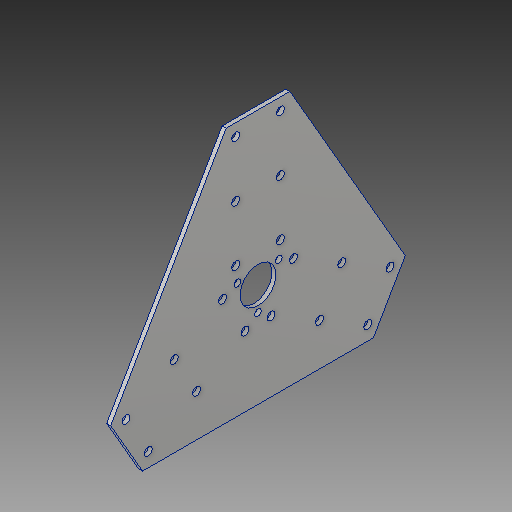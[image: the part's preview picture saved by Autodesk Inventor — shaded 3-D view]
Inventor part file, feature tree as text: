
AUTODESK INVENTOR PART (.ipt)
format: ipt  version: 2019 (Build 230136000, 136)  size: 217,600 bytes
history: native  units: in
note: dims shown in document units (in); Inventor stores cm internally (conversion verified against a paired STEP export)
features: extrude x3, sketch x3, chamfer x1, fillet x1, pattern_circular x1
ambient origin geometry x8: Origin, YZ Plane, XZ Plane, XY Plane, X Axis, Y Axis, Z Axis, Center Point
bodies: Body1 (feature_tree)
feature tree (9):
  extrude  "Extrusion2"  Depth=8.0in
  extrude  "Extrusion3"  Depth=0.125in
  extrude  "Extrusion4"  Depth=0.125in TaperAngle=360.0deg
  chamfer  "Chamfer1"  Distance=1.1547in
  fillet  "Fillet1"  Radius=1.125in
  pattern_circular  "Circular Pattern1"  [2 undecoded]
  sketch  "Sketch1"  dims[d0=8.0in d1=2.0in]
  sketch  "Sketch2"  dims[d2=0.25in d4=0.125in]
  sketch  "Sketch3"  dims[d7=0.7in d8=1.1811in d10=360.0deg d14=1.1547in d15=1.125in d16=0.125in d17=0.0in d18=1.25in d19=30.0deg d20=0.25in d21=1.1811in d23=360.0deg d25=0.21in d26=1.1811in d28=360.0deg d30=0.25in d31=0.0in d32=3.5in d33=0.2996in d34=0.125in d35=0.25in d36=0.125in d37=0.25in d38=0.25in d39=0.25in d40=0.25in d41=0.0in d42=0.125in d43=0.125in d44=45.0deg d45=0.0312in d46=1.1811in d47=360.0deg]
note: 2 required parameter values undecoded (feature->parameter linkage not recoverable at this tier; creation-order binding heuristic only, values carry confidence <= 0.55)
